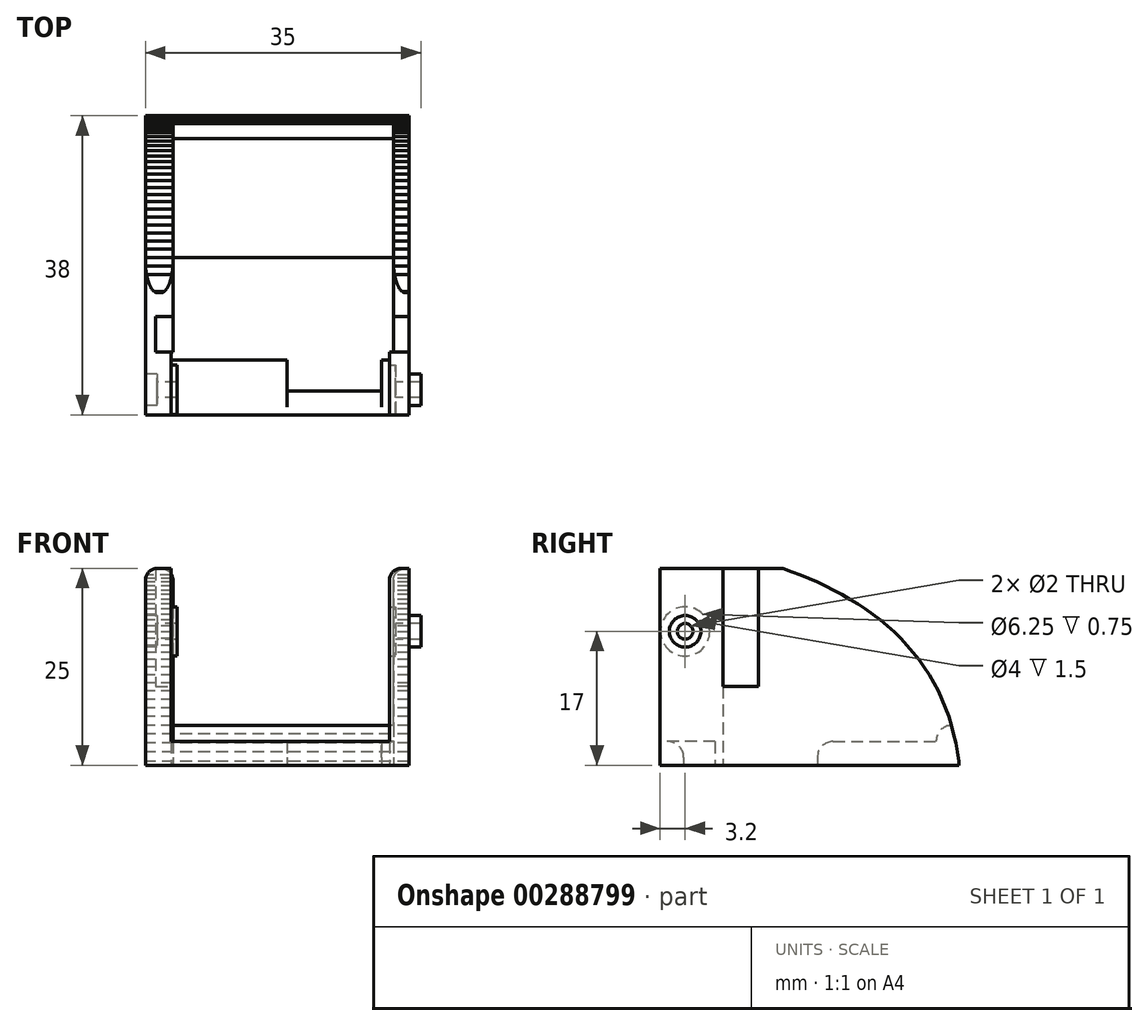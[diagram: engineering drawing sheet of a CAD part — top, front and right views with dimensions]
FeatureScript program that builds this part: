
annotation { "Feature Type Name" : "Feature", "Feature Type Description" : "" }
export const myFeature = defineFeature(function(context is Context, id is Id, definition is map)
    precondition{}
    {
        {
            var Q0;
            Q0=qCreatedBy(makeId("Top.planeOp"),FACE);
            var sketch = newSketch(context, id + "F0", { "sketchPlane" : qUnion([Q0])});
            skLineSegment(sketch, "E0", {"start": v(-17.5, -7) * mm, "end": v(-17.5, 0) * mm});
            skLineSegment(sketch, "E1", {"start": v(-17.5, 0) * mm, "end": v(-17.5, 31) * mm});
            skLineSegment(sketch, "E2", {"start": v(-13.5, 0) * mm, "end": v(13.5, 0) * mm});
            skLineSegment(sketch, "E3", {"start": v(12.5, 0) * mm, "end": v(12.5, -4) * mm});
            skLineSegment(sketch, "E4", {"start": v(12.5, -4) * mm, "end": v(0.5, -4) * mm});
            skLineSegment(sketch, "E5", {"start": v(0.5, -4) * mm, "end": v(0.5, 0) * mm});
            skLineSegment(sketch, "E6", {"start": v(13.5, 0) * mm, "end": v(13.5, -7) * mm});
            skLineSegment(sketch, "E7", {"start": v(13.5, 0) * mm, "end": v(13.5, 1) * mm});
            skLineSegment(sketch, "E8", {"start": v(13.5, 1) * mm, "end": v(16.2, 1) * mm});
            skLineSegment(sketch, "E9", {"start": v(-13.5, 0) * mm, "end": v(-13.5, -7) * mm});
            skLineSegment(sketch, "E10", {"start": v(-16.2, 1) * mm, "end": v(-13.5, 1) * mm});
            skLineSegment(sketch, "E11", {"start": v(-13.5, 1) * mm, "end": v(-13.5, 0) * mm});
            skLineSegment(sketch, "E12", {"start": v(17.5, -7) * mm, "end": v(17.5, 0) * mm});
            skLineSegment(sketch, "E13", {"start": v(17.5, 0) * mm, "end": v(17.5, 31) * mm});
            skLineSegment(sketch, "E14", {"start": v(-17.5, 31) * mm, "end": v(-14, 31) * mm});
            skLineSegment(sketch, "E15", {"start": v(-14, 31) * mm, "end": v(-14, 1) * mm});
            skLineSegment(sketch, "E16", {"start": v(17.5, 31) * mm, "end": v(14, 31) * mm});
            skLineSegment(sketch, "E17", {"start": v(14, 31) * mm, "end": v(14, 1) * mm});
            skLineSegment(sketch, "E18", {"start": v(-16.2, 1) * mm, "end": v(-16.2, 5.5) * mm});
            skLineSegment(sketch, "E19", {"start": v(-16.2, 5.5) * mm, "end": v(-14, 5.5) * mm});
            skLineSegment(sketch, "E20", {"start": v(16.2, 1) * mm, "end": v(16.2, 5.5) * mm});
            skLineSegment(sketch, "E21", {"start": v(16.2, 5.5) * mm, "end": v(14, 5.5) * mm});
            skLineSegment(sketch, "E22", {"start": v(-14, 13) * mm, "end": v(14, 13) * mm});
            skLineSegment(sketch, "E23", {"start": v(-14, 31) * mm, "end": v(14, 31) * mm});
            skLineSegment(sketch, "E24", {"start": v(16.2, 5.5) * mm, "end": v(16.2, 1) * mm});
            skLineSegment(sketch, "E25.trimOffspring", {"start": v(-13.5, -7) * mm, "end": v(17.5, -7) * mm});
            skLineSegment(sketch, "E26", {"start": v(-17.5, -7) * mm, "end": v(-13.5, -7) * mm});
            skSolve(sketch);
        }
        {
            var Q0;
            Q0=makeQuery(id+"F0.imprint","IMPRINT",FACE,{"disambiguationData":[TD([[makeQuery(id+"F0.imprint","IMPRINT",EDGE,{"derivedFrom":sQuery(id+"F0.wireOp",EDGE,"E0")}),-1.0]])]});
            var Q1;
            {var subQ0=sQuery(id+"F0.wireOp",EDGE,"E3");Q1=makeQuery(id+"F0.imprint","IMPRINT",FACE,{"disambiguationData":[TD([[makeQuery(id+"F0.imprint","IMPRINT",EDGE,{"derivedFrom":subQ0}),1.0]])]});}
            var Q2;
            {var subQ5=sQuery(id+"F0.wireOp",EDGE,"E6");Q2=makeQuery(id+"F0.imprint","IMPRINT",FACE,{"disambiguationData":[TD([[makeQuery(id+"F0.imprint","IMPRINT",EDGE,{"derivedFrom":subQ5}),1.0]])]});}
            var Q3;
            {var subQ2=sQuery(id+"F0.wireOp",EDGE,"E22");Q3=makeQuery(id+"F0.imprint","IMPRINT",FACE,{"disambiguationData":[TD([[makeQuery(id+"F0.imprint","IMPRINT",EDGE,{"derivedFrom":subQ2}),1.0]])]});}
            extrude(context, id + "F1", {"entities" : qUnion([Q0, Q1, Q2, Q3]), "depth" : 3 * mm});
        }
        {
            var Q0;
            Q0=makeQuery(id+"F0.imprint","IMPRINT",FACE,{"disambiguationData":[TD([[makeQuery(id+"F0.imprint","IMPRINT",EDGE,{"derivedFrom":sQuery(id+"F0.wireOp",EDGE,"E0")}),-1.0]])]});
            var Q1;
            {var subQ5=sQuery(id+"F0.wireOp",EDGE,"E6");Q1=makeQuery(id+"F0.imprint","IMPRINT",FACE,{"disambiguationData":[TD([[makeQuery(id+"F0.imprint","IMPRINT",EDGE,{"derivedFrom":subQ5}),1.0]])]});}
            extrude(context, id + "F2", {"entities" : qUnion([Q0, Q1]), "operationType" : NewBodyOperationType.ADD, "depth" : 25 * mm});
        }
        {
            var Q0;
            Q0=makeQuery(id+"F1.opExtrude","CAP_EDGE",EDGE,{"disambiguationData":[OSD([sQuery(id+"F0.wireOp",EDGE,"E22")])],"isStart":false});
            var Q1;
            Q1=makeQuery(id+"F1.opExtrude","CAP_EDGE",EDGE,{"disambiguationData":[OSD([sQuery(id+"F0.wireOp",EDGE,"E4")])],"isStart":false});
            fillet(context, id + "F3", {"entities" : qUnion([Q0, Q1]), "radius" : 2 * mm, "tangentPropagation" : true, "allowEdgeOverflow" : false});
        }
        {
            var Q0;
            Q0=makeQuery(id+"F2.opExtrude","SWEPT_FACE",FACE,{"disambiguationData":[OSD([sQuery(id+"F0.wireOp",EDGE,"E6"),sQuery(id+"F0.wireOp",EDGE,"E7")])]});
            var sketch = newSketch(context, id + "F4", { "sketchPlane" : qUnion([Q0])});
            skCircle(sketch, "E27", {"center": v(3.8, 17) * mm, "radius": 1 * mm});
            skCircle(sketch, "E28", {"center": v(3.8, 17) * mm, "radius": 3.12 * mm});
            skSolve(sketch);
        }
        {
            var Q0;
            Q0=makeQuery(id+"F4.imprint","IMPRINT",FACE,{"disambiguationData":[TD([[makeQuery(id+"F4.imprint","IMPRINT",EDGE,{"derivedFrom":sQuery(id+"F4.wireOp",EDGE,"E27")}),1.0]])]});
            var Q1;
            Q1=sQuery(id+"F4.wireOp",EDGE,"E27");
            extrude(context, id + "F5", {"entities" : qUnion([Q0]), "operationType" : NewBodyOperationType.REMOVE, "surfaceEntities" : qUnion([Q1]), "endBound" : BoundingType.SYMMETRIC, "oppositeDirection" : true, "depth" : 100 * mm});
        }
        {
            var Q0;
            {var subQ4=sQuery(id+"F0.wireOp",EDGE,"E21");Q0=makeQuery(id+"F0.imprint","IMPRINT",FACE,{"disambiguationData":[TD([[makeQuery(id+"F0.imprint","IMPRINT",EDGE,{"derivedFrom":subQ4}),1.0]])]});}
            var Q1;
            {var subQ5=sQuery(id+"F0.wireOp",EDGE,"E19");Q1=makeQuery(id+"F0.imprint","IMPRINT",FACE,{"disambiguationData":[TD([[makeQuery(id+"F0.imprint","IMPRINT",EDGE,{"derivedFrom":subQ5}),-1.0]])]});}
            extrude(context, id + "F6", {"entities" : qUnion([Q0, Q1]), "operationType" : NewBodyOperationType.ADD, "depth" : 10 * mm});
        }
        {
            var Q0;
            Q0=makeQuery(id+"F1.boolean.opBoolean","MERGE",FACE,{"derivedFrom":[makeQuery(id+"Fhmbu4aYoJqjBt6_0.opExtrude","SWEPT_FACE",FACE,{"disambiguationData":[OSD([sQuery(id+"F0.wireOp",EDGE,"E1")])]}),makeQuery(id+"F1.opExtrude","SWEPT_FACE",FACE,{"disambiguationData":[OSD([sQuery(id+"F0.wireOp",EDGE,"E0")])]})]});
            var sketch = newSketch(context, id + "F7", { "sketchPlane" : qUnion([Q0])});
            skLineSegment(sketch, "E29", {"start": v(27.07, 29.74) * mm, "end": v(26.71, 29.74) * mm});
            skLineSegment(sketch, "E30", {"start": v(26.71, 29.74) * mm, "end": v(26.29, 29.74) * mm});
            skLineSegment(sketch, "E31", {"start": v(26.29, 29.74) * mm, "end": v(25.8, 29.74) * mm});
            skLineSegment(sketch, "E32", {"start": v(25.8, 29.74) * mm, "end": v(25.27, 29.72) * mm});
            skLineSegment(sketch, "E33", {"start": v(25.27, 29.72) * mm, "end": v(24.72, 29.72) * mm});
            skLineSegment(sketch, "E34", {"start": v(24.72, 29.72) * mm, "end": v(24.1, 29.72) * mm});
            skLineSegment(sketch, "E35", {"start": v(24.1, 29.72) * mm, "end": v(23.5, 29.7) * mm});
            skLineSegment(sketch, "E36", {"start": v(23.5, 29.7) * mm, "end": v(22.84, 29.68) * mm});
            skLineSegment(sketch, "E37", {"start": v(22.84, 29.68) * mm, "end": v(20.17, 29.62) * mm});
            skLineSegment(sketch, "E38", {"start": v(20.17, 29.62) * mm, "end": v(18.86, 29.57) * mm});
            skLineSegment(sketch, "E39", {"start": v(18.86, 29.57) * mm, "end": v(17.63, 29.5) * mm});
            skLineSegment(sketch, "E40", {"start": v(17.63, 29.5) * mm, "end": v(16.45, 29.45) * mm});
            skLineSegment(sketch, "E41", {"start": v(16.45, 29.45) * mm, "end": v(15.3, 29.36) * mm});
            skLineSegment(sketch, "E42", {"start": v(15.3, 29.36) * mm, "end": v(13.06, 29.2) * mm});
            skLineSegment(sketch, "E43", {"start": v(13.06, 29.2) * mm, "end": v(10.8, 28.98) * mm});
            skLineSegment(sketch, "E44", {"start": v(10.8, 28.98) * mm, "end": v(8.49, 28.7) * mm});
            skLineSegment(sketch, "E45", {"start": v(8.49, 28.7) * mm, "end": v(6.16, 28.4) * mm});
            skLineSegment(sketch, "E46", {"start": v(6.16, 28.4) * mm, "end": v(3.83, 28.05) * mm});
            skLineSegment(sketch, "E47", {"start": v(3.83, 28.05) * mm, "end": v(1.5, 27.65) * mm});
            skLineSegment(sketch, "E48", {"start": v(1.5, 27.65) * mm, "end": v(-0.78, 27.16) * mm});
            skLineSegment(sketch, "E49", {"start": v(-0.78, 27.16) * mm, "end": v(-3.05, 26.63) * mm});
            skLineSegment(sketch, "E50", {"start": v(-3.05, 26.63) * mm, "end": v(-5.31, 26.02) * mm});
            skLineSegment(sketch, "E51", {"start": v(-5.31, 26.02) * mm, "end": v(-7.54, 25.34) * mm});
            skLineSegment(sketch, "E52", {"start": v(-7.54, 25.34) * mm, "end": v(-8.64, 24.96) * mm});
            skLineSegment(sketch, "E53", {"start": v(-8.64, 24.96) * mm, "end": v(-9.74, 24.56) * mm});
            skLineSegment(sketch, "E54", {"start": v(-9.74, 24.56) * mm, "end": v(-10.82, 24.15) * mm});
            skLineSegment(sketch, "E55", {"start": v(-10.82, 24.15) * mm, "end": v(-11.9, 23.71) * mm});
            skLineSegment(sketch, "E56", {"start": v(-11.9, 23.71) * mm, "end": v(-12.98, 23.24) * mm});
            skLineSegment(sketch, "E57", {"start": v(-12.98, 23.24) * mm, "end": v(-14.03, 22.74) * mm});
            skLineSegment(sketch, "E58", {"start": v(-14.03, 22.74) * mm, "end": v(-15.07, 22.2) * mm});
            skLineSegment(sketch, "E59", {"start": v(-15.07, 22.2) * mm, "end": v(-16.1, 21.66) * mm});
            skLineSegment(sketch, "E60", {"start": v(-16.1, 21.66) * mm, "end": v(-17.12, 21.06) * mm});
            skLineSegment(sketch, "E61", {"start": v(-17.12, 21.06) * mm, "end": v(-18.12, 20.45) * mm});
            skLineSegment(sketch, "E62", {"start": v(-18.12, 20.45) * mm, "end": v(-19.11, 19.82) * mm});
            skLineSegment(sketch, "E63", {"start": v(-19.11, 19.82) * mm, "end": v(-20.07, 19.14) * mm});
            skLineSegment(sketch, "E64", {"start": v(-20.07, 19.14) * mm, "end": v(-20.98, 18.42) * mm});
            skLineSegment(sketch, "E65", {"start": v(-20.98, 18.42) * mm, "end": v(-21.89, 17.68) * mm});
            skLineSegment(sketch, "E66", {"start": v(-21.89, 17.68) * mm, "end": v(-22.76, 16.9) * mm});
            skLineSegment(sketch, "E67", {"start": v(-22.76, 16.9) * mm, "end": v(-23.58, 16.07) * mm});
            skLineSegment(sketch, "E68", {"start": v(-23.58, 16.07) * mm, "end": v(-24.38, 15.22) * mm});
            skLineSegment(sketch, "E69", {"start": v(-24.38, 15.22) * mm, "end": v(-25.15, 14.33) * mm});
            skLineSegment(sketch, "E70", {"start": v(-25.15, 14.33) * mm, "end": v(-25.89, 13.4) * mm});
            skLineSegment(sketch, "E71", {"start": v(-25.89, 13.4) * mm, "end": v(-26.57, 12.47) * mm});
            skLineSegment(sketch, "E72", {"start": v(-26.57, 12.47) * mm, "end": v(-27.2, 11.48) * mm});
            skLineSegment(sketch, "E73", {"start": v(-27.2, 11.48) * mm, "end": v(-27.8, 10.46) * mm});
            skLineSegment(sketch, "E74", {"start": v(-27.8, 10.46) * mm, "end": v(-28.34, 9.42) * mm});
            skLineSegment(sketch, "E75", {"start": v(-28.34, 9.42) * mm, "end": v(-28.83, 8.36) * mm});
            skLineSegment(sketch, "E76", {"start": v(-28.83, 8.36) * mm, "end": v(-29.27, 7.28) * mm});
            skLineSegment(sketch, "E77", {"start": v(-29.27, 7.28) * mm, "end": v(-29.68, 6.18) * mm});
            skLineSegment(sketch, "E78", {"start": v(-29.68, 6.18) * mm, "end": v(-30.02, 5.06) * mm});
            skLineSegment(sketch, "E79", {"start": v(-30.02, 5.06) * mm, "end": v(-30.31, 3.94) * mm});
            skLineSegment(sketch, "E80", {"start": v(-30.31, 3.94) * mm, "end": v(-30.57, 2.8) * mm});
            skLineSegment(sketch, "E81", {"start": v(-30.57, 2.8) * mm, "end": v(-30.78, 1.65) * mm});
            skLineSegment(sketch, "E82", {"start": v(-30.78, 1.65) * mm, "end": v(-30.95, 0.5) * mm});
            skLineSegment(sketch, "E83", {"start": v(-30.95, 0.5) * mm, "end": v(-31, 0) * mm});
            skLineSegment(sketch, "E84", {"start": v(-31, 0) * mm, "end": v(39, 0) * mm});
            skLineSegment(sketch, "E85", {"start": v(27.07, 29.74) * mm, "end": v(27.07, -0.26) * mm});
            skLineSegment(sketch, "E86.0", {"start": v(-16, 3) * mm, "end": v(-32, 3) * mm});
            skLineSegment(sketch, "E87", {"start": v(-28.08, 3) * mm, "end": v(-28.08, 5.06) * mm});
            skLineSegment(sketch, "E88", {"start": v(-28.08, 5.06) * mm, "end": v(-30.02, 5.06) * mm});
            skPoint(sketch, "E89.0", {"position": v(3.8, 17) * mm});
            skCircle(sketch, "E90", {"center": v(3.8, 17) * mm, "radius": 2 * mm});
            skSolve(sketch);
        }
        {
            var Q0;
            {var subQ0=sQuery(id+"F0.wireOp",EDGE,"E13");var subQ1=sQuery(id+"F0.wireOp",EDGE,"E12");Q0=makeQuery(id+"F2.boolean.opBoolean","MERGE",FACE,{"derivedFrom":[makeQuery(id+"F1.opExtrude","SWEPT_FACE",FACE,{"disambiguationData":[OSD([subQ1,subQ0])]}),makeQuery(id+"F2.opExtrude","SWEPT_FACE",FACE,{"disambiguationData":[OSD([subQ1,subQ0])]})]});}
            var sketch = newSketch(context, id + "F8", { "sketchPlane" : qUnion([Q0])});
            skCircle(sketch, "E91.0", {"center": v(-3.8, 17) * mm, "radius": 2 * mm});
            skSolve(sketch);
        }
        {
            var Q0;
            {var subQ0=sQuery(id+"F7.wireOp",EDGE,"E60");Q0=makeQuery(id+"F7.imprint","IMPRINT",FACE,{"disambiguationData":[TD([[makeQuery(id+"F7.imprint","IMPRINT",EDGE,{"derivedFrom":subQ0}),-1.0]])]});}
            extrude(context, id + "F9", {"entities" : qUnion([Q0]), "operationType" : NewBodyOperationType.REMOVE, "oppositeDirection" : true, "depth" : 100 * mm});
        }
        {
            var Q0;
            Q0=makeQuery(id+"F2.opExtrude","SWEPT_FACE",FACE,{"disambiguationData":[OSD([sQuery(id+"F0.wireOp",EDGE,"E9"),sQuery(id+"F0.wireOp",EDGE,"E11")])]});
            var sketch = newSketch(context, id + "F10", { "sketchPlane" : qUnion([Q0])});
            skCircle(sketch, "E92.0", {"center": v(-3.8, 17) * mm, "radius": 3.12 * mm});
            skSolve(sketch);
        }
        {
            var Q0;
            Q0=makeQuery(id+"F4.imprint","IMPRINT",FACE,{"disambiguationData":[TD([[makeQuery(id+"F4.imprint","IMPRINT",EDGE,{"derivedFrom":sQuery(id+"F4.wireOp",EDGE,"E27")}),-1.0]])]});
            var Q1;
            Q1=makeQuery(id+"F10.imprint","IMPRINT",FACE,{"disambiguationData":[TD([[makeQuery(id+"F10.imprint","IMPRINT",EDGE,{"derivedFrom":sQuery(id+"F10.wireOp",EDGE,"E92.0")}),-1.0]])]});
            extrude(context, id + "F11", {"entities" : qUnion([Q0, Q1]), "operationType" : NewBodyOperationType.REMOVE, "endBound" : BoundingType.SYMMETRIC, "depth" : 1.5 * mm});
        }
        {
            var Q0;
            Q0=makeQuery(id+"F2.opExtrude","CAP_EDGE",EDGE,{"disambiguationData":[OSD([sQuery(id+"F0.wireOp",EDGE,"E12"),sQuery(id+"F0.wireOp",EDGE,"E13")])],"isStart":false});
            var Q1;
            Q1=makeQuery(id+"F2.opExtrude","CAP_EDGE",EDGE,{"disambiguationData":[OSD([sQuery(id+"F0.wireOp",EDGE,"E17")])],"isStart":false});
            var Q2;
            Q2=makeQuery(id+"F2.opExtrude","CAP_EDGE",EDGE,{"disambiguationData":[OSD([sQuery(id+"F0.wireOp",EDGE,"E6"),sQuery(id+"F0.wireOp",EDGE,"E7")])],"isStart":false});
            var Q3;
            Q3=makeQuery(id+"F2.opExtrude","CAP_EDGE",EDGE,{"disambiguationData":[OSD([sQuery(id+"F0.wireOp",EDGE,"E0"),sQuery(id+"F0.wireOp",EDGE,"E1")])],"isStart":false});
            var Q4;
            Q4=makeQuery(id+"F2.opExtrude","CAP_EDGE",EDGE,{"disambiguationData":[OSD([sQuery(id+"F0.wireOp",EDGE,"E9"),sQuery(id+"F0.wireOp",EDGE,"E11")])],"isStart":false});
            var Q5;
            Q5=makeQuery(id+"F2.opExtrude","CAP_EDGE",EDGE,{"disambiguationData":[OSD([sQuery(id+"F0.wireOp",EDGE,"E15")])],"isStart":false});
            fillet(context, id + "F12", {"entities" : qUnion([Q0, Q1, Q2, Q3, Q4, Q5]), "radius" : 1.5 * mm, "tangentPropagation" : true, "allowEdgeOverflow" : false});
        }
        {
            var Q0;
            {var subQ4=sQuery(id+"F7.wireOp",EDGE,"E79");Q0=makeQuery(id+"F7.imprint","IMPRINT",FACE,{"disambiguationData":[TD([[makeQuery(id+"F7.imprint","IMPRINT",EDGE,{"derivedFrom":subQ4}),1.0]])]});}
            extrude(context, id + "F13", {"entities" : qUnion([Q0]), "operationType" : NewBodyOperationType.ADD, "oppositeDirection" : true, "depth" : 35 * mm});
        }
        {
            var Q0;
            {var subQ6=sQuery(id+"F7.wireOp",EDGE,"E81");Q0=makeQuery(id+"F7.imprint","IMPRINT",FACE,{"disambiguationData":[TD([[makeQuery(id+"F7.imprint","IMPRINT",EDGE,{"derivedFrom":subQ6}),-1.0]])]});}
            extrude(context, id + "F14", {"entities" : qUnion([Q0]), "operationType" : NewBodyOperationType.REMOVE, "oppositeDirection" : true, "depth" : 39 * mm});
        }
        {
            var Q0;
            Q0=makeQuery(id+"F13.opExtrude","SWEPT_EDGE",EDGE,{"disambiguationData":[OSD([sQuery(id+"F7.wireOp",EDGE,"E87"),sQuery(id+"F7.wireOp",EDGE,"E88")])]});
            fillet(context, id + "F15", {"entities" : qUnion([Q0]), "radius" : 2 * mm, "tangentPropagation" : true, "allowEdgeOverflow" : false});
        }
        {
            var Q0;
            Q0=makeQuery(id+"F7.imprint","IMPRINT",FACE,{"disambiguationData":[TD([[makeQuery(id+"F7.imprint","IMPRINT",EDGE,{"derivedFrom":sQuery(id+"F7.wireOp",EDGE,"E90")}),1.0]])]});
            var Q1;
            Q1=makeQuery(id+"F8.imprint","IMPRINT",FACE,{"disambiguationData":[TD([[makeQuery(id+"F8.imprint","IMPRINT",EDGE,{"derivedFrom":sQuery(id+"F8.wireOp",EDGE,"E91.0")}),-1.0]])]});
            extrude(context, id + "F16", {"entities" : qUnion([Q0, Q1]), "operationType" : NewBodyOperationType.REMOVE, "endBound" : BoundingType.SYMMETRIC, "oppositeDirection" : true, "depth" : 3 * mm});
        }
    });
